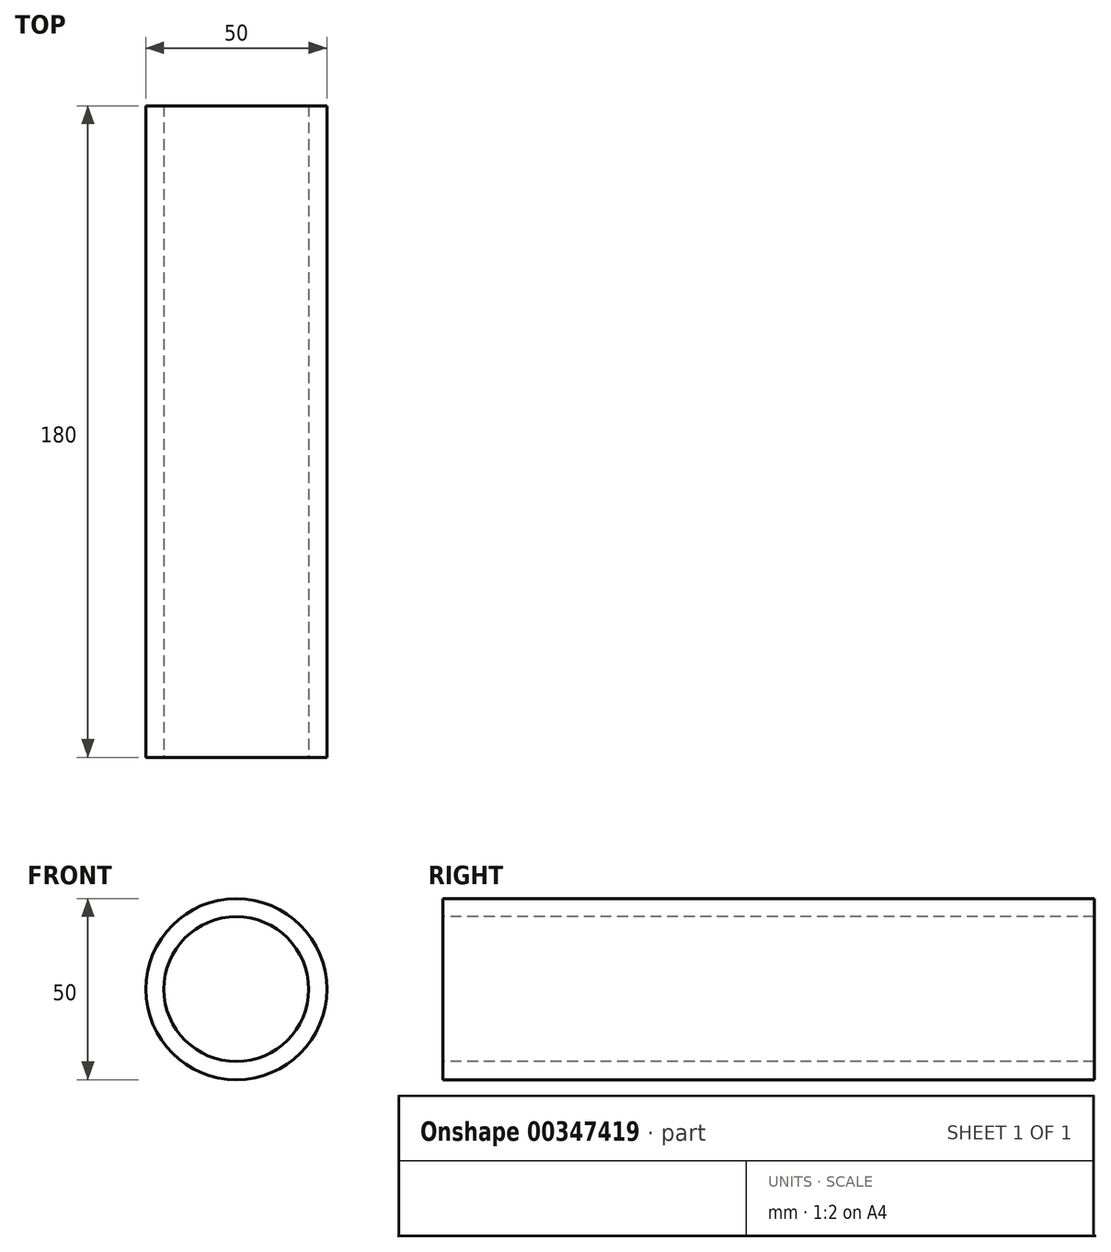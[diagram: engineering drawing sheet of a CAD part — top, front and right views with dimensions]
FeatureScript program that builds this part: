
annotation { "Feature Type Name" : "Feature", "Feature Type Description" : "" }
export const myFeature = defineFeature(function(context is Context, id is Id, definition is map)
    precondition{}
    {
        {
            var Q0;
            Q0=qCreatedBy(makeId("Front.planeOp"),FACE);
            var sketch = newSketch(context, id + "F0", { "sketchPlane" : qUnion([Q0])});
            skCircle(sketch, "E0", {"center": v(-35.82, 57.27) * mm, "radius": 25 * mm});
            skSolve(sketch);
        }
        {
            var Q0;
            Q0 = qSketchRegion(id + "F0", true);
            extrude(context, id + "F1", {"entities" : qUnion([Q0]), "depth" : 180 * mm});
        }
        {
            var Q0;
            Q0=makeQuery(id+"F1.opExtrude","CAP_FACE",FACE,{"disambiguationData":[OSD([sQuery(id+"F0.wireOp",EDGE,"E0")])],"isStart":false});
            var sketch = newSketch(context, id + "F2", { "sketchPlane" : qUnion([Q0])});
            skCircle(sketch, "E1", {"center": v(-35.82, 57.27) * mm, "radius": 20 * mm});
            skSolve(sketch);
        }
        {
            var Q0;
            Q0=sQuery(id+"F2.wireOp",VERTEX,"E1.center");
            var Q1;
            Q1=makeQuery(id+"F1.opExtrude","SWEPT_BODY",BODY,{"disambiguationData":[OSD([sQuery(id+"F0.wireOp",EDGE,"E0")])]});
            hole(context, id + "F3", {"style" : HoleStyle.SIMPLE, "endStyle" : HoleEndStyle.THROUGH, "holeDiameter" : 40 * mm, "isTappedThrough" : true, "tappedDepth" : 12 * mm, "tapClearance" : 3, "locations" : qUnion([Q0]), "scope" : qUnion([Q1])});
        }
    });
